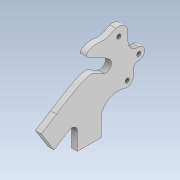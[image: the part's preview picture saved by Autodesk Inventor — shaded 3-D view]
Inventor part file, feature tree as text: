
AUTODESK INVENTOR PART (.ipt)
format: ipt  version: 2021 (Build 250183000, 183)  size: 151,552 bytes
history: native  units: mm
features: sketch x3, hole x2, other x1, extrude x1
ambient origin geometry x8: Origin, YZ Plane, XZ Plane, XY Plane, X Axis, Y Axis, Z Axis, Center Point
bodies: Body1 (feature_tree)
feature tree (7):
  other  "Sólido1"
  extrude  "Extrusión1"  Depth=10.0mm TaperAngle=0.0deg
  hole  "Agujero1"  [1 undecoded]
  hole  "Agujero2"  [1 undecoded]
  sketch  "Boceto1"  dims[d0=20.0mm d1=7.391063mm d2=15.0mm d3=9.526623mm d4=15.0mm d5=10.0mm d6=10.0mm d7=60.109139mm d8=50.0mm d9=5.0mm d10=0.0mm]
  sketch  "Boceto2"  dims[d11=3.4mm d12=6.0mm d13=6.3mm d14=2.0mm d15=90.0deg d16=8.0mm d17=20.594885mm]
  sketch  "Boceto3"  dims[d18=3.4mm d19=6.0mm d20=6.3mm d21=2.0mm d22=90.0deg d23=8.0mm d24=20.594885mm]
note: 2 required parameter values undecoded (feature->parameter linkage not recoverable at this tier; creation-order binding heuristic only, values carry confidence <= 0.55)
